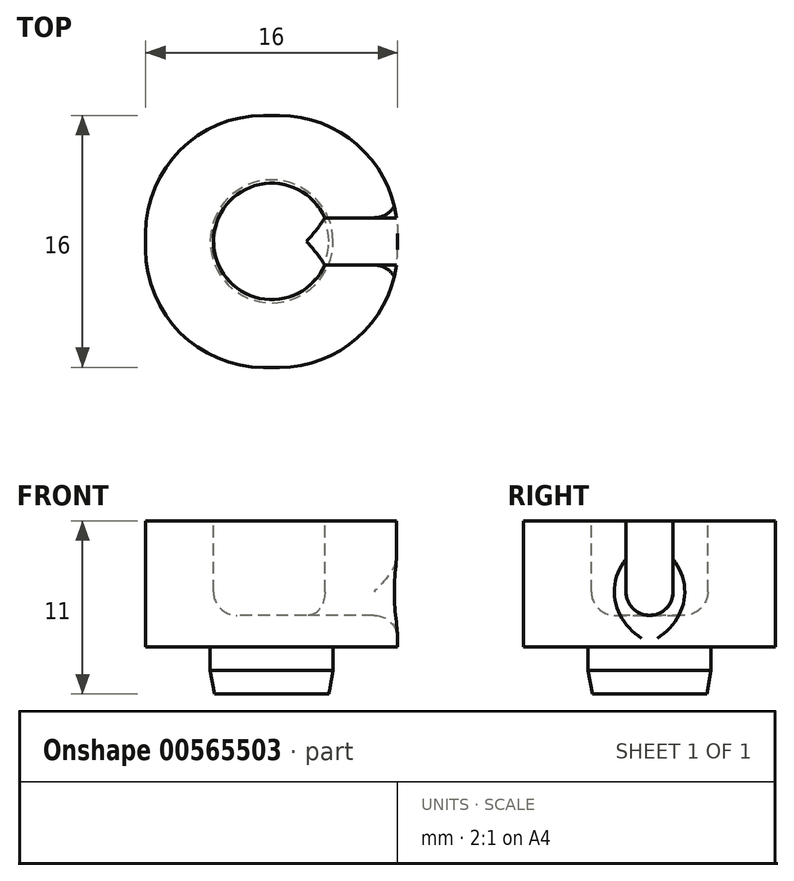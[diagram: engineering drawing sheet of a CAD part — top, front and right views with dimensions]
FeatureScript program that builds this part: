
annotation { "Feature Type Name" : "Feature", "Feature Type Description" : "" }
export const myFeature = defineFeature(function(context is Context, id is Id, definition is map)
    precondition{}
    {
        {
            var Q0;
            Q0=qCreatedBy(makeId("Top.planeOp"),FACE);
            var sketch = newSketch(context, id + "F0", { "sketchPlane" : qUnion([Q0])});
            skCircle(sketch, "E0", {"center": v(0, 0) * mm, "radius": 3.9 * mm});
            skSolve(sketch);
        }
        {
            var Q0;
            Q0 = qSketchRegion(id + "F0", true);
            extrude(context, id + "F1", {"entities" : qUnion([Q0]), "depth" : 3 * mm, "offsetDistance" : 25 * mm});
        }
        {
            var Q0;
            Q0=makeQuery(id+"F1.opExtrude","CAP_FACE",FACE,{"disambiguationData":[OSD([sQuery(id+"F0.wireOp",EDGE,"E0")])],"isStart":false});
            var sketch = newSketch(context, id + "F2", { "sketchPlane" : qUnion([Q0])});
            skLineSegment(sketch, "E1.bottom", {"start": v(-8, 8) * mm, "end": v(8, 8) * mm});
            skLineSegment(sketch, "E1.top", {"start": v(-8, -8) * mm, "end": v(8, -8) * mm});
            skLineSegment(sketch, "E1.left", {"start": v(-8, 8) * mm, "end": v(-8, -8) * mm});
            skLineSegment(sketch, "E1.right", {"start": v(8, 8) * mm, "end": v(8, -8) * mm});
            skPoint(sketch, "E1.middle", {"position": v(0, 0) * mm});
            skSolve(sketch);
        }
        {
            var Q0;
            Q0 = qSketchRegion(id + "F2", true);
            extrude(context, id + "F3", {"entities" : qUnion([Q0]), "operationType" : NewBodyOperationType.ADD, "depth" : 8 * mm, "offsetDistance" : 25 * mm});
        }
        {
            var Q0;
            Q0=makeQuery(id+"F3.opExtrude","CAP_FACE",FACE,{"disambiguationData":[OSD([sQuery(id+"F2.wireOp",EDGE,"E1.bottom"),sQuery(id+"F2.wireOp",EDGE,"E1.top"),sQuery(id+"F2.wireOp",EDGE,"E1.left"),sQuery(id+"F2.wireOp",EDGE,"E1.right")])],"isStart":false});
            var sketch = newSketch(context, id + "F4", { "sketchPlane" : qUnion([Q0])});
            skCircle(sketch, "E2", {"center": v(0, 0) * mm, "radius": 3.7 * mm});
            skSolve(sketch);
        }
        {
            var Q0;
            Q0 = qSketchRegion(id + "F4", true);
            extrude(context, id + "F5", {"entities" : qUnion([Q0]), "operationType" : NewBodyOperationType.REMOVE, "oppositeDirection" : true, "depth" : 6 * mm, "offsetDistance" : 25 * mm});
        }
        {
            var Q0;
            Q0=makeQuery(id+"F3.opExtrude","CAP_FACE",FACE,{"disambiguationData":[OSD([sQuery(id+"F2.wireOp",EDGE,"E1.bottom"),sQuery(id+"F2.wireOp",EDGE,"E1.top"),sQuery(id+"F2.wireOp",EDGE,"E1.left"),sQuery(id+"F2.wireOp",EDGE,"E1.right")])],"isStart":false});
            var sketch = newSketch(context, id + "F6", { "sketchPlane" : qUnion([Q0])});
            skLineSegment(sketch, "E3.bottom", {"start": v(3.38, 1.5) * mm, "end": v(8, 1.5) * mm});
            skLineSegment(sketch, "E3.top", {"start": v(3.38, -1.5) * mm, "end": v(8, -1.5) * mm});
            skLineSegment(sketch, "E3.left", {"start": v(3.38, 1.5) * mm, "end": v(3.38, -1.5) * mm});
            skLineSegment(sketch, "E3.right", {"start": v(8, 1.5) * mm, "end": v(8, -1.5) * mm});
            skSolve(sketch);
        }
        {
            var Q0;
            Q0 = qSketchRegion(id + "F6", true);
            extrude(context, id + "F7", {"entities" : qUnion([Q0]), "operationType" : NewBodyOperationType.REMOVE, "oppositeDirection" : true, "depth" : 6 * mm, "offsetDistance" : 25 * mm});
        }
        {
            var Q0;
            Q0=makeQuery(id+"F7.boolean.opBoolean","MERGE",FACE,{"derivedFrom":[makeQuery(id+"F5.boolean.opBoolean","COPY",FACE,{"derivedFrom":makeQuery(id+"F5.opExtrude","CAP_FACE",FACE,{"disambiguationData":[OSD([sQuery(id+"F4.wireOp",EDGE,"E2")])],"isStart":false})}),makeQuery(id+"F7.opExtrude","CAP_FACE",FACE,{"disambiguationData":[OSD([sQuery(id+"F6.wireOp",EDGE,"E3.bottom"),sQuery(id+"F6.wireOp",EDGE,"E3.top"),sQuery(id+"F6.wireOp",EDGE,"E3.left"),sQuery(id+"F6.wireOp",EDGE,"E3.right")])],"isStart":false})]});
            fillet(context, id + "F8", {"entities" : qUnion([Q0]), "radius" : 1.5 * mm, "tangentPropagation" : true, "allowEdgeOverflow" : false});
        }
        {
            var Q0;
            Q0=makeQuery(id+"F1.opExtrude","CAP_EDGE",EDGE,{"disambiguationData":[OSD([sQuery(id+"F0.wireOp",EDGE,"E0")])],"isStart":true});
            chamfer(context, id + "F9", {"entities" : qUnion([Q0]), "chamferType" : ChamferType.OFFSET_ANGLE, "width" : 1.5 * mm, "oppositeDirection" : false, "angle" : 10 * degree, "tangentPropagation" : true});
        }
        {
            var Q0;
            Q0=makeQuery(id+"F3.opExtrude","SWEPT_EDGE",EDGE,{"disambiguationData":[OSD([sQuery(id+"F2.wireOp",EDGE,"E1.top"),sQuery(id+"F2.wireOp",EDGE,"E1.right")])]});
            var Q1;
            Q1=makeQuery(id+"F3.opExtrude","SWEPT_EDGE",EDGE,{"disambiguationData":[OSD([sQuery(id+"F2.wireOp",EDGE,"E1.top"),sQuery(id+"F2.wireOp",EDGE,"E1.left")])]});
            var Q2;
            Q2=makeQuery(id+"F3.opExtrude","SWEPT_EDGE",EDGE,{"disambiguationData":[OSD([sQuery(id+"F2.wireOp",EDGE,"E1.bottom"),sQuery(id+"F2.wireOp",EDGE,"E1.right")])]});
            var Q3;
            Q3=makeQuery(id+"F3.opExtrude","SWEPT_EDGE",EDGE,{"disambiguationData":[OSD([sQuery(id+"F2.wireOp",EDGE,"E1.bottom"),sQuery(id+"F2.wireOp",EDGE,"E1.left")])]});
            fillet(context, id + "F10", {"entities" : qUnion([Q0, Q1, Q2, Q3]), "radius" : 7.5 * mm, "tangentPropagation" : true, "allowEdgeOverflow" : false});
        }
    });
